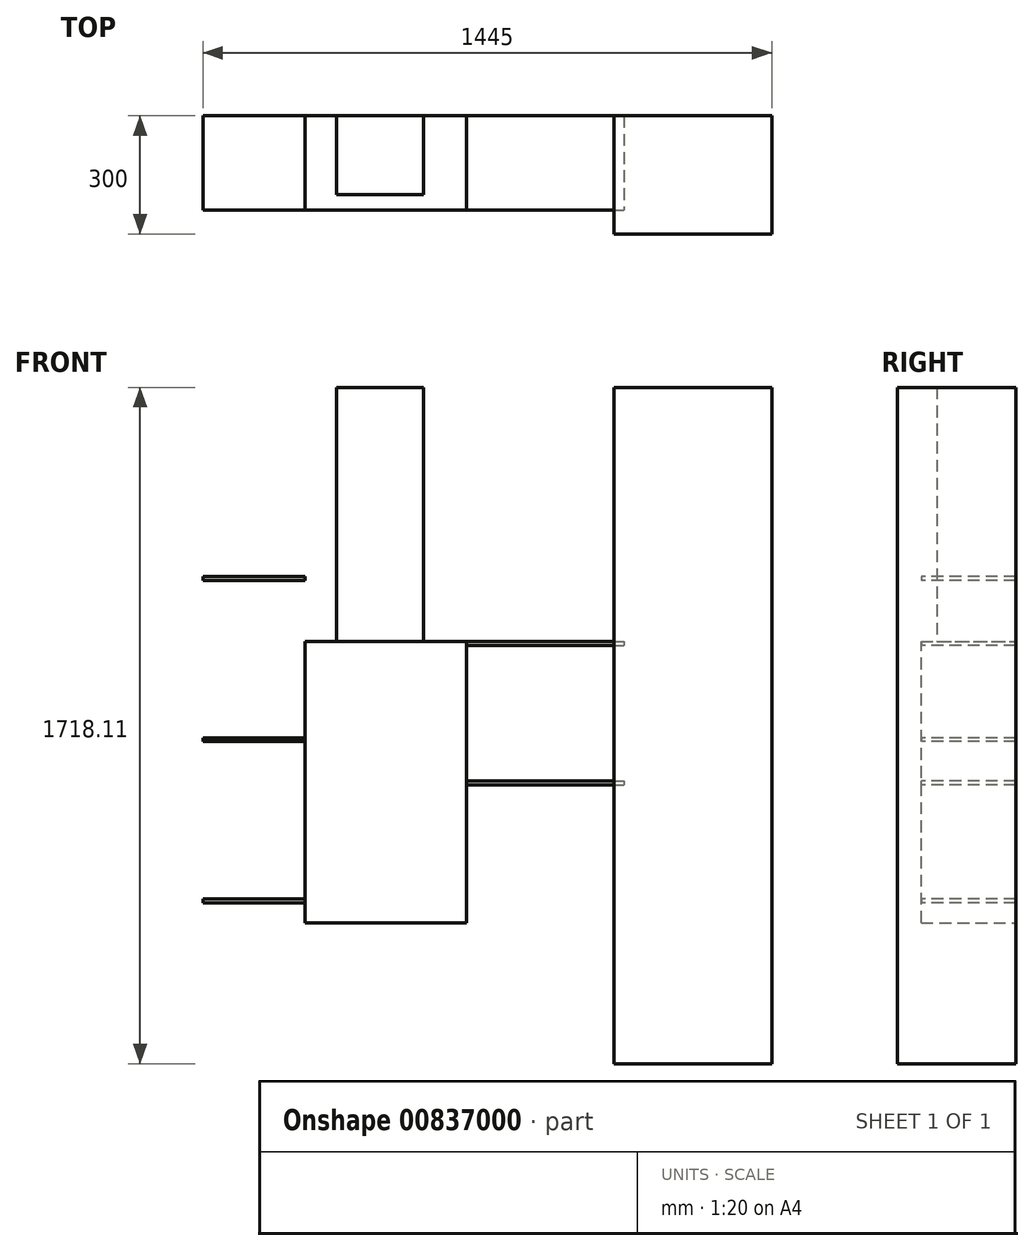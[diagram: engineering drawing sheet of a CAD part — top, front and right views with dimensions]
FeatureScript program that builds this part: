
annotation { "Feature Type Name" : "Feature", "Feature Type Description" : "" }
export const myFeature = defineFeature(function(context is Context, id is Id, definition is map)
    precondition{}
    {
        {
            var Q0;
            Q0=qCreatedBy(makeId("Front.planeOp"),FACE);
            var sketch = newSketch(context, id + "F0", { "sketchPlane" : qUnion([Q0])});
            skLineSegment(sketch, "E0.bottom", {"start": v(-522.5, 860) * mm, "end": v(522.5, 860) * mm});
            skLineSegment(sketch, "E0.top", {"start": v(-522.5, -860) * mm, "end": v(522.5, -860) * mm});
            skLineSegment(sketch, "E0.left", {"start": v(-522.5, 860) * mm, "end": v(-522.5, -860) * mm});
            skLineSegment(sketch, "E0.right", {"start": v(522.5, 860) * mm, "end": v(522.5, -860) * mm});
            skPoint(sketch, "E0.middle", {"position": v(0, 0) * mm});
            skLineSegment(sketch, "E1.bottom", {"start": v(-262.5, -500) * mm, "end": v(147.5, -500) * mm});
            skLineSegment(sketch, "E1.top", {"start": v(-262.5, 215) * mm, "end": v(147.5, 215) * mm});
            skLineSegment(sketch, "E1.left", {"start": v(-262.5, -500) * mm, "end": v(-262.5, 215) * mm});
            skLineSegment(sketch, "E1.right", {"start": v(147.5, -500) * mm, "end": v(147.5, 215) * mm});
            skLineSegment(sketch, "E2.bottom", {"start": v(522.5, 860) * mm, "end": v(922.5, 860) * mm});
            skLineSegment(sketch, "E2.top", {"start": v(522.5, -858.11) * mm, "end": v(922.5, -858.11) * mm});
            skLineSegment(sketch, "E2.left", {"start": v(522.5, 860) * mm, "end": v(522.5, -858.11) * mm});
            skLineSegment(sketch, "E2.right", {"start": v(922.5, 860) * mm, "end": v(922.5, -858.11) * mm});
            skLineSegment(sketch, "E3.bottom", {"start": v(-182.5, 860) * mm, "end": v(37.5, 860) * mm});
            skLineSegment(sketch, "E3.top", {"start": v(-182.5, 215) * mm, "end": v(37.5, 215) * mm});
            skLineSegment(sketch, "E3.left", {"start": v(-182.5, 860) * mm, "end": v(-182.5, 215) * mm});
            skLineSegment(sketch, "E3.right", {"start": v(37.5, 860) * mm, "end": v(37.5, 215) * mm});
            skLineSegment(sketch, "E4.bottom", {"start": v(-522.5, 860) * mm, "end": v(-622.5, 860) * mm});
            skLineSegment(sketch, "E4.top", {"start": v(-522.5, -860) * mm, "end": v(-622.5, -860) * mm});
            skLineSegment(sketch, "E4.right", {"start": v(-622.5, 860) * mm, "end": v(-622.5, -860) * mm});
            skSolve(sketch);
        }
        {
            var Q0;
            {var subQ0=sQuery(id+"F0.wireOp",EDGE,"E2.bottom");Q0=makeQuery(id+"F0.imprint","IMPRINT",FACE,{"disambiguationData":[TD([[makeQuery(id+"F0.imprint","IMPRINT",EDGE,{"derivedFrom":subQ0}),-1.0]])]});}
            extrude(context, id + "F1", {"entities" : qUnion([Q0]), "depth" : 300 * mm, "offsetDistance" : 25 * mm});
        }
        {
            var Q0;
            Q0=makeQuery(id+"F0.imprint","IMPRINT",FACE,{"disambiguationData":[TD([[makeQuery(id+"F0.imprint","IMPRINT",EDGE,{"derivedFrom":sQuery(id+"F0.wireOp",EDGE,"E1.bottom")}),1.0]])]});
            extrude(context, id + "F2", {"entities" : qUnion([Q0]), "depth" : 240 * mm, "offsetDistance" : 25 * mm});
        }
        {
            var Q0;
            {var subQ2=sQuery(id+"F0.wireOp",EDGE,"E3.left");Q0=makeQuery(id+"F0.imprint","IMPRINT",FACE,{"disambiguationData":[TD([[makeQuery(id+"F0.imprint","IMPRINT",EDGE,{"derivedFrom":subQ2}),1.0]])]});}
            extrude(context, id + "F3", {"entities" : qUnion([Q0]), "operationType" : NewBodyOperationType.ADD, "depth" : 200 * mm, "offsetDistance" : 25 * mm});
        }
        {
            var Q0;
            Q0=makeQuery(id+"F2.opExtrude","CAP_FACE",FACE,{"disambiguationData":[OSD([sQuery(id+"F0.wireOp",EDGE,"E1.bottom"),sQuery(id+"F0.wireOp",EDGE,"E1.top"),sQuery(id+"F0.wireOp",EDGE,"E1.left"),sQuery(id+"F0.wireOp",EDGE,"E1.right")])],"isStart":false});
            var sketch = newSketch(context, id + "F4", { "sketchPlane" : qUnion([Q0])});
            skLineSegment(sketch, "E5.bottom", {"start": v(-522.5, -440) * mm, "end": v(-262.5, -440) * mm});
            skLineSegment(sketch, "E5.top", {"start": v(-522.5, -450) * mm, "end": v(-262.5, -450) * mm});
            skLineSegment(sketch, "E5.left", {"start": v(-522.5, -440) * mm, "end": v(-522.5, -450) * mm});
            skLineSegment(sketch, "E5.right", {"start": v(-262.5, -440) * mm, "end": v(-262.5, -450) * mm});
            skLineSegment(sketch, "E6.bottom", {"start": v(-522.5, -30) * mm, "end": v(-262.5, -30) * mm});
            skLineSegment(sketch, "E6.top", {"start": v(-522.5, -40) * mm, "end": v(-262.5, -40) * mm});
            skLineSegment(sketch, "E6.left", {"start": v(-522.5, -30) * mm, "end": v(-522.5, -40) * mm});
            skLineSegment(sketch, "E6.right", {"start": v(-262.5, -30) * mm, "end": v(-262.5, -40) * mm});
            skLineSegment(sketch, "E7.bottom", {"start": v(-522.5, 380) * mm, "end": v(-262.5, 380) * mm});
            skLineSegment(sketch, "E7.top", {"start": v(-522.5, 370) * mm, "end": v(-262.5, 370) * mm});
            skLineSegment(sketch, "E7.left", {"start": v(-522.5, 380) * mm, "end": v(-522.5, 370) * mm});
            skLineSegment(sketch, "E7.right", {"start": v(-262.5, 380) * mm, "end": v(-262.5, 370) * mm});
            skLineSegment(sketch, "E8.bottom", {"start": v(147.5, -140) * mm, "end": v(522.5, -140) * mm});
            skLineSegment(sketch, "E8.top", {"start": v(147.5, -150) * mm, "end": v(522.5, -150) * mm});
            skLineSegment(sketch, "E8.left", {"start": v(147.5, -140) * mm, "end": v(147.5, -150) * mm});
            skLineSegment(sketch, "E8.right", {"start": v(522.5, -140) * mm, "end": v(522.5, -150) * mm});
            skLineSegment(sketch, "E9.0.1.0", {"start": v(522.5, 215) * mm, "end": v(522.5, 205) * mm});
            skLineSegment(sketch, "E9.0.1.1", {"start": v(147.5, 205) * mm, "end": v(522.5, 205) * mm});
            skLineSegment(sketch, "E9.0.1.2", {"start": v(147.5, 215) * mm, "end": v(522.5, 215) * mm});
            skLineSegment(sketch, "E9.0.1.3", {"start": v(147.5, 215) * mm, "end": v(147.5, 205) * mm});
            skLineSegment(sketch, "E9.1.0.0", {"start": v(547.5, -140) * mm, "end": v(547.5, -150) * mm});
            skLineSegment(sketch, "E9.1.0.1", {"start": v(172.5, -150) * mm, "end": v(547.5, -150) * mm});
            skLineSegment(sketch, "E9.1.0.2", {"start": v(172.5, -140) * mm, "end": v(547.5, -140) * mm});
            skLineSegment(sketch, "E9.1.0.3", {"start": v(172.5, -140) * mm, "end": v(172.5, -150) * mm});
            skLineSegment(sketch, "E9.1.1.0", {"start": v(547.5, 215) * mm, "end": v(547.5, 205) * mm});
            skLineSegment(sketch, "E9.1.1.1", {"start": v(172.5, 205) * mm, "end": v(547.5, 205) * mm});
            skLineSegment(sketch, "E9.1.1.2", {"start": v(172.5, 215) * mm, "end": v(547.5, 215) * mm});
            skLineSegment(sketch, "E9.1.1.3", {"start": v(172.5, 215) * mm, "end": v(172.5, 205) * mm});
            skLineSegment(sketch, "E9.2.0.0", {"start": v(572.5, -140) * mm, "end": v(572.5, -150) * mm});
            skLineSegment(sketch, "E9.2.0.1", {"start": v(197.5, -150) * mm, "end": v(572.5, -150) * mm});
            skLineSegment(sketch, "E9.2.0.2", {"start": v(197.5, -140) * mm, "end": v(572.5, -140) * mm});
            skLineSegment(sketch, "E9.2.0.3", {"start": v(197.5, -140) * mm, "end": v(197.5, -150) * mm});
            skLineSegment(sketch, "E9.2.1.0", {"start": v(572.5, 215) * mm, "end": v(572.5, 205) * mm});
            skLineSegment(sketch, "E9.2.1.1", {"start": v(197.5, 205) * mm, "end": v(572.5, 205) * mm});
            skLineSegment(sketch, "E9.2.1.2", {"start": v(197.5, 215) * mm, "end": v(572.5, 215) * mm});
            skLineSegment(sketch, "E9.2.1.3", {"start": v(197.5, 215) * mm, "end": v(197.5, 205) * mm});
            skLineSegment(sketch, "E9.direction1", {"start": v(147.5, -150) * mm, "end": v(172.5, -150) * mm, "construction": true});
            skLineSegment(sketch, "E9.direction2", {"start": v(147.5, -150) * mm, "end": v(147.5, 205) * mm, "construction": true});
            skSolve(sketch);
        }
        {
            var Q0;
            {var subQ3=sQuery(id+"F4.wireOp",EDGE,"E5.right");Q0=makeQuery(id+"F4.imprint","IMPRINT",FACE,{"disambiguationData":[TD([[makeQuery(id+"F4.imprint","IMPRINT",EDGE,{"derivedFrom":subQ3}),-1.0]])]});}
            var sketch = newSketch(context, id + "F5", { "sketchPlane" : qUnion([Q0])});
            skLineSegment(sketch, "E10.bottom", {"start": v(-522.5, 860) * mm, "end": v(147.5, 860) * mm});
            skLineSegment(sketch, "E10.top", {"start": v(-522.5, -640) * mm, "end": v(147.5, -640) * mm});
            skLineSegment(sketch, "E10.left", {"start": v(-522.5, 860) * mm, "end": v(-522.5, -640) * mm});
            skLineSegment(sketch, "E10.right", {"start": v(147.5, 860) * mm, "end": v(147.5, -640) * mm});
            skLineSegment(sketch, "E11.bottom", {"start": v(147.5, 860) * mm, "end": v(522.5, 860) * mm});
            skLineSegment(sketch, "E11.top", {"start": v(147.5, -140) * mm, "end": v(522.5, -140) * mm});
            skLineSegment(sketch, "E11.left", {"start": v(147.5, 860) * mm, "end": v(147.5, -140) * mm});
            skLineSegment(sketch, "E11.right", {"start": v(522.5, 860) * mm, "end": v(522.5, -140) * mm});
            skSolve(sketch);
        }
        {
            var Q0;
            Q0=makeQuery(id+"F4.imprint","IMPRINT",FACE,{"disambiguationData":[TD([[makeQuery(id+"F4.imprint","IMPRINT",EDGE,{"derivedFrom":sQuery(id+"F4.wireOp",EDGE,"E7.bottom")}),-1.0]])]});
            var Q1;
            Q1=makeQuery(id+"F4.imprint","IMPRINT",FACE,{"disambiguationData":[TD([[makeQuery(id+"F4.imprint","IMPRINT",EDGE,{"derivedFrom":sQuery(id+"F4.wireOp",EDGE,"E6.bottom")}),-1.0]])]});
            var Q2;
            Q2=makeQuery(id+"F4.imprint","IMPRINT",FACE,{"disambiguationData":[TD([[makeQuery(id+"F4.imprint","IMPRINT",EDGE,{"derivedFrom":sQuery(id+"F4.wireOp",EDGE,"E5.bottom")}),-1.0]])]});
            var Q3;
            {var subQ0=sQuery(id+"F4.wireOp",EDGE,"E9.0.1.0");Q3=makeQuery(id+"F4.imprint","IMPRINT",FACE,{"disambiguationData":[TD([[makeQuery(id+"F4.imprint","IMPRINT",EDGE,{"derivedFrom":subQ0}),-1.0]])]});}
            var Q4;
            Q4=makeQuery(id+"F4.imprint","IMPRINT",FACE,{"disambiguationData":[TD([[makeQuery(id+"F4.imprint","IMPRINT",EDGE,{"derivedFrom":sQuery(id+"F4.wireOp",EDGE,"E9.1.1.1")}),1.0]])]});
            var Q5;
            Q5=makeQuery(id+"F4.imprint","IMPRINT",FACE,{"disambiguationData":[TD([[makeQuery(id+"F4.imprint","IMPRINT",EDGE,{"derivedFrom":sQuery(id+"F4.wireOp",EDGE,"E9.0.1.1")}),1.0]])]});
            var Q6;
            {var subQ0=sQuery(id+"F4.wireOp",EDGE,"E8.right");Q6=makeQuery(id+"F4.imprint","IMPRINT",FACE,{"disambiguationData":[TD([[makeQuery(id+"F4.imprint","IMPRINT",EDGE,{"derivedFrom":subQ0}),-1.0]])]});}
            var Q7;
            Q7=makeQuery(id+"F4.imprint","IMPRINT",FACE,{"disambiguationData":[TD([[makeQuery(id+"F4.imprint","IMPRINT",EDGE,{"derivedFrom":sQuery(id+"F4.wireOp",EDGE,"E9.1.0.1")}),1.0]])]});
            var Q8;
            Q8=makeQuery(id+"F4.imprint","IMPRINT",FACE,{"disambiguationData":[TD([[makeQuery(id+"F4.imprint","IMPRINT",EDGE,{"derivedFrom":sQuery(id+"F4.wireOp",EDGE,"E8.bottom")}),-1.0]])]});
            extrude(context, id + "F6", {"entities" : qUnion([Q0, Q1, Q2, Q3, Q4, Q5, Q6, Q7, Q8]), "oppositeDirection" : true, "depth" : 240 * mm, "offsetDistance" : 25 * mm});
        }
    });
